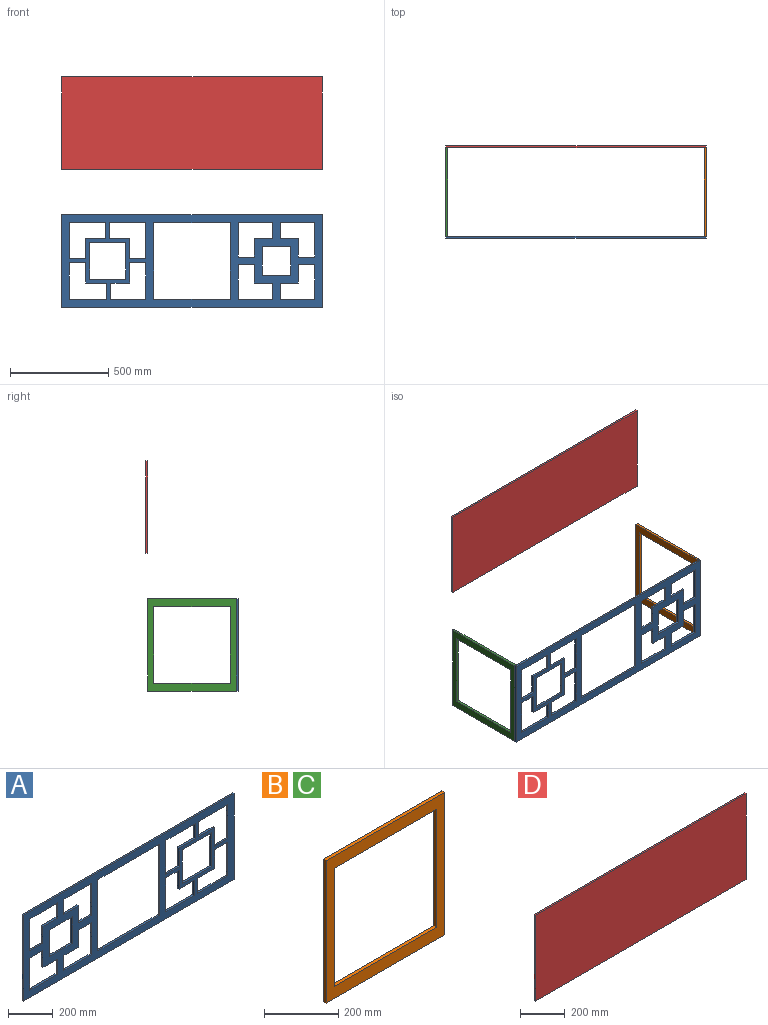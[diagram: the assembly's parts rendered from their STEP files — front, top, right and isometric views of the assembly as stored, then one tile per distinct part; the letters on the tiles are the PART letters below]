
ASSEMBLY  parts=4 mates=9
PART A: 66 faces, bbox 1330x10x470 mm
  f0: plane 1330x470mm, normal (0,-1,0), area 234600mm2, adj f2,f3,f4,f5,f6,f7,f8,f9
  f1: plane 1330x470mm, normal (0,1,0), area 234600mm2, adj f2,f3,f4,f5,f6,f7,f8,f9
  f2: plane 470x10mm, normal (-1,0,0), area 4700mm2, adj f0,f1,f3,f5
  f3: plane 1330x10mm, normal (0,0,-1), area 13300mm2, adj f0,f1,f2,f4
  f4: plane 470x10mm, normal (1,0,0), area 4700mm2, adj f0,f1,f3,f5
  f5: plane 1330x10mm, normal (0,0,1), area 13300mm2, adj f0,f1,f2,f4
  f6: plane 390x10mm, normal (0,0,-1), area 3900mm2, adj f0,f1,f7,f9
  f7: plane 390x10mm, normal (1,0,0), area 3900mm2, adj f0,f1,f6,f8
  f8: plane 390x10mm, normal (0,0,1), area 3900mm2, adj f0,f1,f7,f9
  f9: plane 390x10mm, normal (-1,0,0), area 3900mm2, adj f0,f1,f6,f8
  f10: plane 179.19x10mm, normal (0,0,1), area 1791.9mm2, adj f0,f1,f11,f15
  f11: plane 82.5x10mm, normal (-1,0,0), area 825mm2, adj f0,f1,f10,f12
  f12: plane 96.69x10mm, normal (0,0,-1), area 966.9mm2, adj f0,f1,f11,f13
  f13: plane 102.5x10mm, normal (-1,0,0), area 1025mm2, adj f0,f1,f12,f14
  f14: plane 82.5x10mm, normal (0,0,-1), area 825mm2, adj f0,f1,f13,f15
  f15: plane 185x10mm, normal (1,0,0), area 1850mm2, adj f0,f1,f10,f14
  f16: plane 185x10mm, normal (0,0,-1), area 1850mm2, adj f0,f1,f17,f19
  f17: plane 185x10mm, normal (1,0,0), area 1850mm2, adj f0,f1,f16,f18
  f18: plane 185x10mm, normal (0,0,1), area 1850mm2, adj f0,f1,f17,f19
  f19: plane 185x10mm, normal (-1,0,0), area 1850mm2, adj f0,f1,f16,f18
  f20: plane 82.5x10mm, normal (-1,0,0), area 825mm2, adj f0,f1,f21,f25
  f21: plane 175x10mm, normal (0,0,-1), area 1750mm2, adj f0,f1,f20,f22
  f22: plane 175x10mm, normal (1,0,0), area 1750mm2, adj f0,f1,f21,f23
  f23: plane 82.5x10mm, normal (0,0,1), area 825mm2, adj f0,f1,f22,f24
  f24: plane 92.5x10mm, normal (-1,0,0), area 925mm2, adj f0,f1,f23,f25
  f25: plane 92.5x10mm, normal (0,0,1), area 925mm2, adj f0,f1,f20,f24
  f26: plane 82.5x10mm, normal (1,0,0), area 825mm2, adj f0,f1,f27,f31
  f27: plane 92.5x10mm, normal (0,0,1), area 925mm2, adj f0,f1,f26,f28
  f28: plane 92.5x10mm, normal (1,0,0), area 925mm2, adj f0,f1,f27,f29
  f29: plane 82.5x10mm, normal (0,0,1), area 825mm2, adj f0,f1,f28,f30
  f30: plane 175x10mm, normal (-1,0,0), area 1750mm2, adj f0,f1,f29,f31
  f31: plane 175x10mm, normal (0,0,-1), area 1750mm2, adj f0,f1,f26,f30
  f32: plane 175x10mm, normal (-1,0,0), area 1750mm2, adj f0,f1,f33,f37
  f33: plane 82.5x10mm, normal (0,0,-1), area 825mm2, adj f0,f1,f32,f34
  f34: plane 92.5x10mm, normal (1,0,0), area 925mm2, adj f0,f1,f33,f35
  f35: plane 92.5x10mm, normal (0,0,-1), area 925mm2, adj f0,f1,f34,f36
  f36: plane 82.5x10mm, normal (1,0,0), area 825mm2, adj f0,f1,f35,f37
  f37: plane 175x10mm, normal (0,0,1), area 1750mm2, adj f0,f1,f32,f36
  f38: plane 175x10mm, normal (0,0,1), area 1750mm2, adj f0,f1,f39,f43
  f39: plane 82.5x10mm, normal (-1,0,0), area 825mm2, adj f0,f1,f38,f40
  f40: plane 92.5x10mm, normal (0,0,-1), area 925mm2, adj f0,f1,f39,f41
  f41: plane 92.5x10mm, normal (-1,0,0), area 925mm2, adj f0,f1,f40,f42
  f42: plane 82.5x10mm, normal (0,0,-1), area 825mm2, adj f0,f1,f41,f43
  f43: plane 175x10mm, normal (1,0,0), area 1750mm2, adj f0,f1,f38,f42
  f44: plane 145x10mm, normal (0,0,-1), area 1450mm2, adj f0,f1,f45,f47
  f45: plane 145x10mm, normal (1,0,0), area 1450mm2, adj f0,f1,f44,f46
  f46: plane 145x10mm, normal (0,0,1), area 1450mm2, adj f0,f1,f45,f47
  f47: plane 145x10mm, normal (-1,0,0), area 1450mm2, adj f0,f1,f44,f46
  f48: plane 82.5x10mm, normal (-1,0,0), area 825mm2, adj f0,f1,f49,f53
  f49: plane 185x10mm, normal (0,0,-1), area 1850mm2, adj f0,f1,f48,f50
  f50: plane 185x10mm, normal (1,0,0), area 1850mm2, adj f0,f1,f49,f51
  f51: plane 82.5x10mm, normal (0,0,1), area 825mm2, adj f0,f1,f50,f52
  f52: plane 102.5x10mm, normal (-1,0,0), area 1025mm2, adj f0,f1,f51,f53
  f53: plane 102.5x10mm, normal (0,0,1), area 1025mm2, adj f0,f1,f48,f52
  f54: plane 185x10mm, normal (0,0,-1), area 1850mm2, adj f0,f1,f55,f59
  f55: plane 82.5x10mm, normal (1,0,0), area 825mm2, adj f0,f1,f54,f56
  f56: plane 102.5x10mm, normal (0,0,1), area 1025mm2, adj f0,f1,f55,f57
  f57: plane 102.5x10mm, normal (1,0,0), area 1025mm2, adj f0,f1,f56,f58
  f58: plane 82.5x10mm, normal (0,0,1), area 825mm2, adj f0,f1,f57,f59
  f59: plane 185x10mm, normal (-1,0,0), area 1850mm2, adj f0,f1,f54,f58
  f60: plane 82.5x10mm, normal (1,0,0), area 825mm2, adj f0,f1,f61,f65
  f61: plane 190.81x10mm, normal (0,0,1), area 1908.1mm2, adj f0,f1,f60,f62
  f62: plane 185x10mm, normal (-1,0,0), area 1850mm2, adj f0,f1,f61,f63
  f63: plane 82.5x10mm, normal (0,0,-1), area 825mm2, adj f0,f1,f62,f64
  f64: plane 102.5x10mm, normal (1,0,0), area 1025mm2, adj f0,f1,f63,f65
  f65: plane 108.31x10mm, normal (0,0,-1), area 1083.1mm2, adj f0,f1,f60,f64
PART B: 10 faces, bbox 450x10x470 mm
  f0: plane 470x450mm, normal (0,-1,0), area 59400mm2, adj f2,f3,f4,f5,f6,f7,f8,f9
  f1: plane 470x450mm, normal (0,1,0), area 59400mm2, adj f2,f3,f4,f5,f6,f7,f8,f9
  f2: plane 450x10mm, normal (0,0,-1), area 4500mm2, adj f0,f1,f3,f5
  f3: plane 470x10mm, normal (1,0,0), area 4700mm2, adj f0,f1,f2,f4
  f4: plane 450x10mm, normal (0,0,1), area 4500mm2, adj f0,f1,f3,f5
  f5: plane 470x10mm, normal (-1,0,0), area 4700mm2, adj f0,f1,f2,f4
  f6: plane 390x10mm, normal (0,0,-1), area 3900mm2, adj f0,f1,f7,f9
  f7: plane 390x10mm, normal (1,0,0), area 3900mm2, adj f0,f1,f6,f8
  f8: plane 390x10mm, normal (0,0,1), area 3900mm2, adj f0,f1,f7,f9
  f9: plane 390x10mm, normal (-1,0,0), area 3900mm2, adj f0,f1,f6,f8
PART C: same geometry as B
PART D: 6 faces, bbox 1330x10x470 mm
  f0: plane 1330x10mm, normal (0,0,1), area 13300mm2, adj f1,f3,f4,f5
  f1: plane 470x10mm, normal (-1,0,0), area 4700mm2, adj f0,f2,f4,f5
  f2: plane 1330x10mm, normal (0,0,-1), area 13300mm2, adj f1,f3,f4,f5
  f3: plane 470x10mm, normal (1,0,0), area 4700mm2, adj f0,f2,f4,f5
  f4: plane 1330x470mm, normal (0,-1,0), area 625100mm2, adj f0,f1,f2,f3
  f5: plane 1330x470mm, normal (0,1,0), area 625100mm2, adj f0,f1,f2,f3
PLACE A rot(axis=(0,0,-1),180deg) t=(2910.44,-920.75,-1097.35)mm
PLACE B rot(axis=(0,0,-1),90deg) t=(2910.44,-1060.75,-1097.35)mm
PLACE C rot(axis=(0,0,1),90deg) t=(1580.44,-310.75,-1097.35)mm
PLACE D t=(1580.44,-450.75,225.48)mm
MATE planar C.f1 <-> A.f4  axis (-1,0,0) through (1580.44,-685.75,-862.35)mm
MATE planar D.f4 <-> B.f5  axis (0,-1,0) through (2245.44,-460.75,-159.52)mm
MATE planar C.f3 <-> D.f4  axis (0,1,0) through (1585.44,-460.75,-862.35)mm
MATE planar C.f1 <-> D.f1  axis (-1,0,0) through (1580.44,-685.75,-862.35)mm
MATE planar B.f4 <-> A.f5  axis (0,0,1) through (2905.44,-685.75,-627.35)mm
MATE planar C.f4 <-> A.f5  axis (0,0,1) through (1585.44,-685.75,-627.35)mm
MATE planar B.f1 <-> A.f2  axis (1,0,0) through (2910.44,-685.75,-862.35)mm
MATE planar C.f5 <-> A.f0  axis (0,-1,0) through (1585.44,-910.75,-862.35)mm
MATE planar A.f0 <-> B.f3  axis (0,1,0) through (2281.77,-910.75,-862.35)mm
